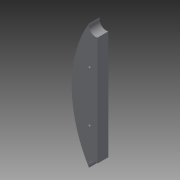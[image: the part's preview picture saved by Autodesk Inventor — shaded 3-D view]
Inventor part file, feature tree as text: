
AUTODESK INVENTOR PART (.ipt)
format: ipt  version: 2015 (Build 190159000, 159)  size: 88,064 bytes
history: native  units: mm
features: extrude x1, sketch x1
ambient origin geometry x8: Origin, YZ Plane, XZ Plane, XY Plane, X Axis, Y Axis, Z Axis, Center Point
bodies: Body1 (feature_tree)
feature tree (2):
  extrude  "Extrusion5"  Depth=13.0mm
  sketch  "Sketch1"  dims[d13=35.0mm d14=35.35mm d17=3.0mm d21=3.0mm d24=31.0mm d27=65.5mm d28=65.5mm d35=14.0mm d36=8.0mm d37=14.0mm d38=8.0mm d39=13.0mm d40=0.0mm]
